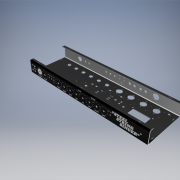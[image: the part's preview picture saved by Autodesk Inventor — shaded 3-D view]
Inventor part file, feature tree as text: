
AUTODESK INVENTOR PART (.ipt)
format: ipt  version: 2018.1 (Build 221171000, 171)  size: 1,857,024 bytes
history: native  units: in
note: dims shown in document units (in); Inventor stores cm internally (conversion verified against a paired STEP export)
features: other x22, sheet_metal_op x13, sketch x12
ambient origin geometry x8: Origin, YZ Plane, XZ Plane, XY Plane, X Axis, Y Axis, Z Axis, Center Point
bodies: Solid1 (feature_tree)
feature tree (47):
  other  "Blocks"
  sheet_metal_op  "Face1"
  sheet_metal_op  "Flange1"
  sheet_metal_op  "Flange2"
  sketch  "Sketch9"  dims[d5=0.125in]
  sketch  "Sketch10"  dims[d6=0.0625in]
  sheet_metal_op  "Flange9"
  sheet_metal_op  "Flange10"
  sketch  "Sketch21"  dims[d14=0.125in]
  other  "Decal1"
  other  "Decal2"
  sketch  "Sketch2"  dims[d2=26.5in]
  other  "Plate1"
  sketch  "Sketch3"  dims[d3=8.5in]
  other  "Plate2"
  sheet_metal_op  "Bend1"
  sheet_metal_op  "Corner1"
  sketch  "Sketch4"  dims[d4=0.125in]
  other  "Plate3"
  sheet_metal_op  "Bend2"
  sheet_metal_op  "Corner2"
  sketch  "Sketch13"  dims[d7=0.25in]
  other  "Plate10"
  sheet_metal_op  "Bend9"
  sheet_metal_op  "Corner9"
  sketch  "Sketch14"  dims[d8=0.125in]
  other  "Plate11"
  sheet_metal_op  "Bend10"
  sheet_metal_op  "Corner10"
  sketch  "Sketch17"  dims[d12=0.5in]
  sketch  "Sketch18"  dims[d13=0.125in]
  other  "A$C2850429B"
  other  "A$C2850429B_1"
  other  "A$C2850429B_2"
  sketch  "Sketch22"  dims[d15=0.125in d16=0.0625in d17=0.25in d18=0.125in d19=2.75in d20=90.0deg d21=0.125in d22=0.5in d23=0.125in d24=0.125in d65=0.125in d66=0.0in d87=0.125in d88=0.0625in d89=0.25in d90=0.125in d91=0.75in d92=90.0deg d93=0.125in d94=0.5in d95=0.125in d96=0.125in d97=0.125in d98=0.0625in d99=0.25in d100=0.125in d101=0.75in d102=90.0deg d103=0.125in d104=0.5in d105=0.125in d106=0.125in d118=0.125in d119=0.0in d120=0.125in d121=0.125in d142=0.125in d143=0.0in d144=0.125in d145=0.0in d148=0.125in d149=0.0in]
  other  "Image1"
  other  "Image2"
  other  "Cut1"
  sketch  "Sketch16"  dims[d9=2.75in d10=90.0deg d11=0.125in]
  other  "Cut3"
  other  "Cut4"
  other  "Cut6"
  other  "Definition1"
  other  "Cut2"
  other  "Annotations"
  other  "Linear Dimension 1"
  other  "Linear Dimension 2"
